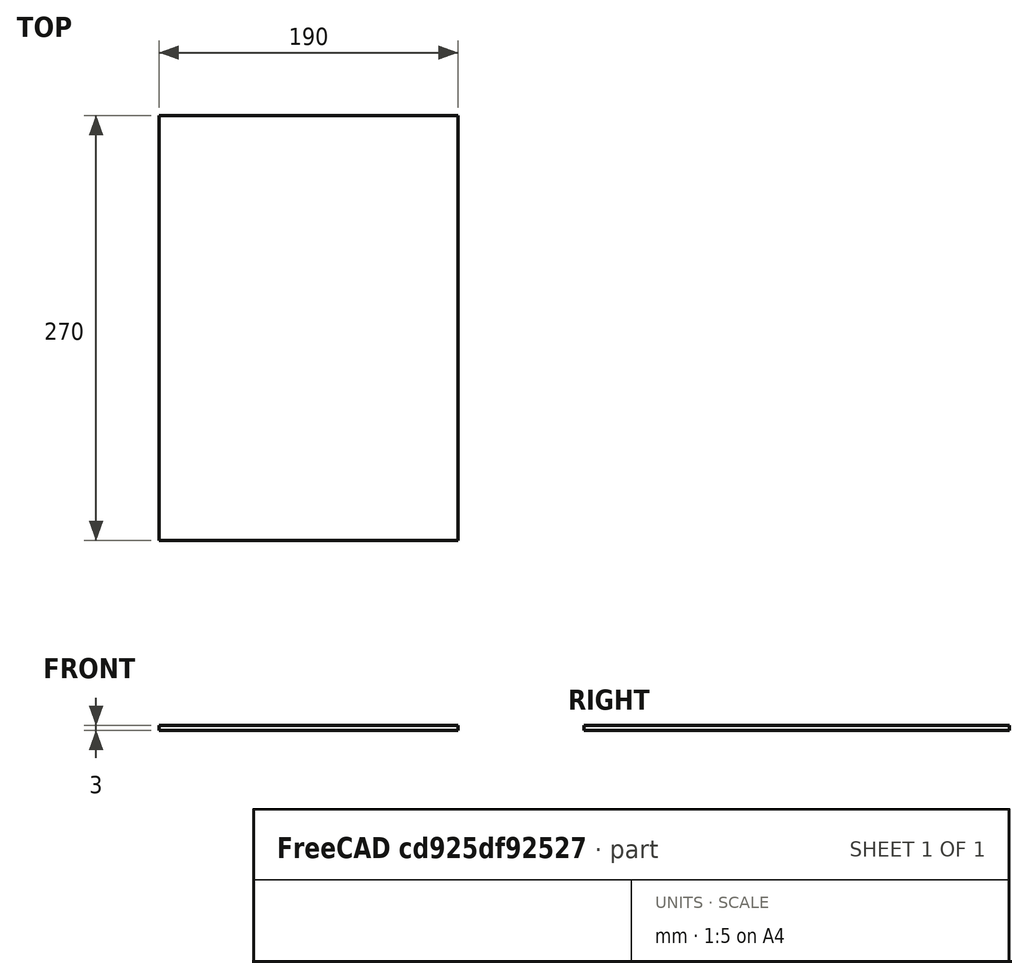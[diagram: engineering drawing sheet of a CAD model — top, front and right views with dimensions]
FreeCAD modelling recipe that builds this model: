
FCSTD DOCUMENT  (FreeCAD 0.19R24291 (Git))
Label: layout
License: All rights reserved
LicenseURL: http://en.wikipedia.org/wiki/All_rights_reserved
objects: Sketcher::SketchObject×2, PartDesign::Pad×1, PartDesign::Body×1
note: 5 computed .brp shape members not serialized (recipe doc carries the construction recipe); baked Part::Feature solids carry a one-line shape summary decoded from their .brp

FEATURE [Sketcher::SketchObject] Sketch
  FullyConstrained = true
  MapMode = 5
  Support = -> [XY_Plane]
  sketch-geometry (4):
    g0: LineSegment StartX=0 StartY=0 StartZ=0 EndX=-190 EndY=0 EndZ=0
    g1: LineSegment StartX=-190 StartY=0 StartZ=0 EndX=-190 EndY=270 EndZ=0
    g2: LineSegment StartX=-190 StartY=270 StartZ=0 EndX=0 EndY=270 EndZ=0
    g3: LineSegment StartX=0 StartY=270 StartZ=0 EndX=0 EndY=0 EndZ=0
  constraints (11):
    c: Coincident(g0,g1)
    c: Coincident(g1,g2)
    c: Coincident(g2,g3)
    c: Coincident(g3,g0)
    c: Horizontal(g0)
    c: Horizontal(g2)
    c: Vertical(g1)
    c: Vertical(g3)
    c: Coincident(g0,g-1)
    c: DistanceY(g1,g1) = 270
    c: DistanceX(g0,g0) = 190
FEATURE [PartDesign::Pad] Pad
  Direction = (1,1,1)
  Length = 3
  Length2 = 100
  Profile = -> Sketch
  Type = 0
FEATURE [Sketcher::SketchObject] Sketch001
  FullyConstrained = false
  MapMode = 5
  Placement = pos=(0,0,3) rot=(0,0,1;0rad)
  Support = -> [Pad]
  sketch-geometry (28):
    g0: LineSegment StartX=-185.711 StartY=265.413 StartZ=0 EndX=-95.7114 EndY=265.413 EndZ=0
    g1: LineSegment StartX=-95.7114 StartY=265.413 StartZ=0 EndX=-95.7114 EndY=205.413 EndZ=0
    g2: LineSegment StartX=-95.7114 StartY=205.413 StartZ=0 EndX=-185.711 EndY=205.413 EndZ=0
    g3: LineSegment StartX=-185.711 StartY=205.413 StartZ=0 EndX=-185.711 EndY=265.413 EndZ=0
    g4: LineSegment StartX=-73.8122 StartY=265.183 StartZ=0 EndX=-3.81215 EndY=265.183 EndZ=0
    g5: LineSegment StartX=-3.81215 StartY=265.183 StartZ=0 EndX=-3.81215 EndY=205.183 EndZ=0
    g6: LineSegment StartX=-3.81215 StartY=205.183 StartZ=0 EndX=-73.8122 EndY=205.183 EndZ=0
    g7: LineSegment StartX=-73.8122 StartY=205.183 StartZ=0 EndX=-73.8122 EndY=265.183 EndZ=0
    g8: LineSegment StartX=-148.15 StartY=105.37 StartZ=0 EndX=-8.15033 EndY=105.37 EndZ=0
    g9: LineSegment StartX=-8.15033 StartY=105.37 StartZ=0 EndX=-8.15033 EndY=45.3703 EndZ=0
    g10: LineSegment StartX=-8.15033 StartY=45.3703 StartZ=0 EndX=-148.15 EndY=45.3703 EndZ=0
    g11: LineSegment StartX=-148.15 StartY=45.3703 StartZ=0 EndX=-148.15 EndY=105.37 EndZ=0
    g12: LineSegment StartX=-185.969 StartY=193.287 StartZ=0 EndX=-85.9695 EndY=193.287 EndZ=0
    g13: LineSegment StartX=-85.9695 StartY=193.287 StartZ=0 EndX=-85.9695 EndY=123.287 EndZ=0
    g14: LineSegment StartX=-85.9695 StartY=123.287 StartZ=0 EndX=-185.969 EndY=123.287 EndZ=0
    g15: LineSegment StartX=-185.969 StartY=123.287 StartZ=0 EndX=-185.969 EndY=193.287 EndZ=0
    g16: LineSegment StartX=-75.7906 StartY=192.453 StartZ=0 EndX=-30.7906 EndY=192.453 EndZ=0
    g17: LineSegment StartX=-30.7906 StartY=192.453 StartZ=0 EndX=-30.7906 EndY=167.453 EndZ=0
    g18: LineSegment StartX=-30.7906 StartY=167.453 StartZ=0 EndX=-75.7906 EndY=167.453 EndZ=0
    g19: LineSegment StartX=-75.7906 StartY=167.453 StartZ=0 EndX=-75.7906 EndY=192.453 EndZ=0
    g20: LineSegment StartX=-76.2256 StartY=159.917 StartZ=0 EndX=-21.2256 EndY=159.917 EndZ=0
    g21: LineSegment StartX=-21.2256 StartY=159.917 StartZ=0 EndX=-21.2256 EndY=114.917 EndZ=0
    g22: LineSegment StartX=-21.2256 StartY=114.917 StartZ=0 EndX=-76.2256 EndY=114.917 EndZ=0
    g23: LineSegment StartX=-76.2256 StartY=114.917 StartZ=0 EndX=-76.2256 EndY=159.917 EndZ=0
    g24: LineSegment StartX=-176.842 StartY=21.6037 StartZ=0 EndX=-116.842 EndY=21.6037 EndZ=0
    g25: LineSegment StartX=-116.842 StartY=21.6037 StartZ=0 EndX=-116.842 EndY=1.60366 EndZ=0
    g26: LineSegment StartX=-116.842 StartY=1.60366 StartZ=0 EndX=-176.842 EndY=1.60366 EndZ=0
    g27: LineSegment StartX=-176.842 StartY=1.60366 StartZ=0 EndX=-176.842 EndY=21.6037 EndZ=0
  constraints (70):
    c: Coincident(g0,g1)
    c: Coincident(g1,g2)
    c: Coincident(g2,g3)
    c: Coincident(g3,g0)
    c: Horizontal(g0)
    c: Horizontal(g2)
    c: Vertical(g1)
    c: Vertical(g3)
    c: DistanceX(g2,g2) = 90
    c: DistanceY(g3,g3) = 60
    c: Coincident(g4,g5)
    c: Coincident(g5,g6)
    c: Coincident(g6,g7)
    c: Coincident(g7,g4)
    c: Horizontal(g4)
    c: Horizontal(g6)
    c: Vertical(g5)
    c: Vertical(g7)
    c: DistanceY(g5,g5) = 60
    c: DistanceX(g6,g6) = 70
    c: Coincident(g8,g9)
    c: Coincident(g9,g10)
    c: Coincident(g10,g11)
    c: Coincident(g11,g8)
    c: Horizontal(g8)
    c: Horizontal(g10)
    c: Vertical(g9)
    c: Vertical(g11)
    c: DistanceX(g10,g10) = 140
    c: DistanceY(g9,g9) = 60
    c: Coincident(g12,g13)
    c: Coincident(g13,g14)
    c: Coincident(g14,g15)
    c: Coincident(g15,g12)
    c: Horizontal(g12)
    c: Horizontal(g14)
    c: Vertical(g13)
    c: Vertical(g15)
    c: DistanceX(g14,g14) = 100
    c: DistanceY(g15,g15) = 70
    c: Coincident(g16,g17)
    c: Coincident(g17,g18)
    c: Coincident(g18,g19)
    c: Coincident(g19,g16)
    c: Horizontal(g16)
    c: Horizontal(g18)
    c: Vertical(g17)
    c: Vertical(g19)
    c: DistanceX(g16,g16) = 45
    c: DistanceY(g19,g19) = 25
    c: Coincident(g20,g21)
    c: Coincident(g21,g22)
    c: Coincident(g22,g23)
    c: Coincident(g23,g20)
    c: Horizontal(g20)
    c: Horizontal(g22)
    c: Vertical(g21)
    c: Vertical(g23)
    c: DistanceX(g22,g22) = 55
    c: DistanceY(g23,g23) = 45
    c: Coincident(g24,g25)
    c: Coincident(g25,g26)
    c: Coincident(g26,g27)
    c: Coincident(g27,g24)
    c: Horizontal(g24)
    c: Horizontal(g26)
    c: Vertical(g25)
    c: Vertical(g27)
    c: DistanceX(g26,g26) = 60
    c: DistanceY(g25,g25) = 20
FEATURE [PartDesign::Body] Body
  Group = -> [Sketch,Pad,Sketch001]
  Origin = -> Origin
  Tip = -> Pad
